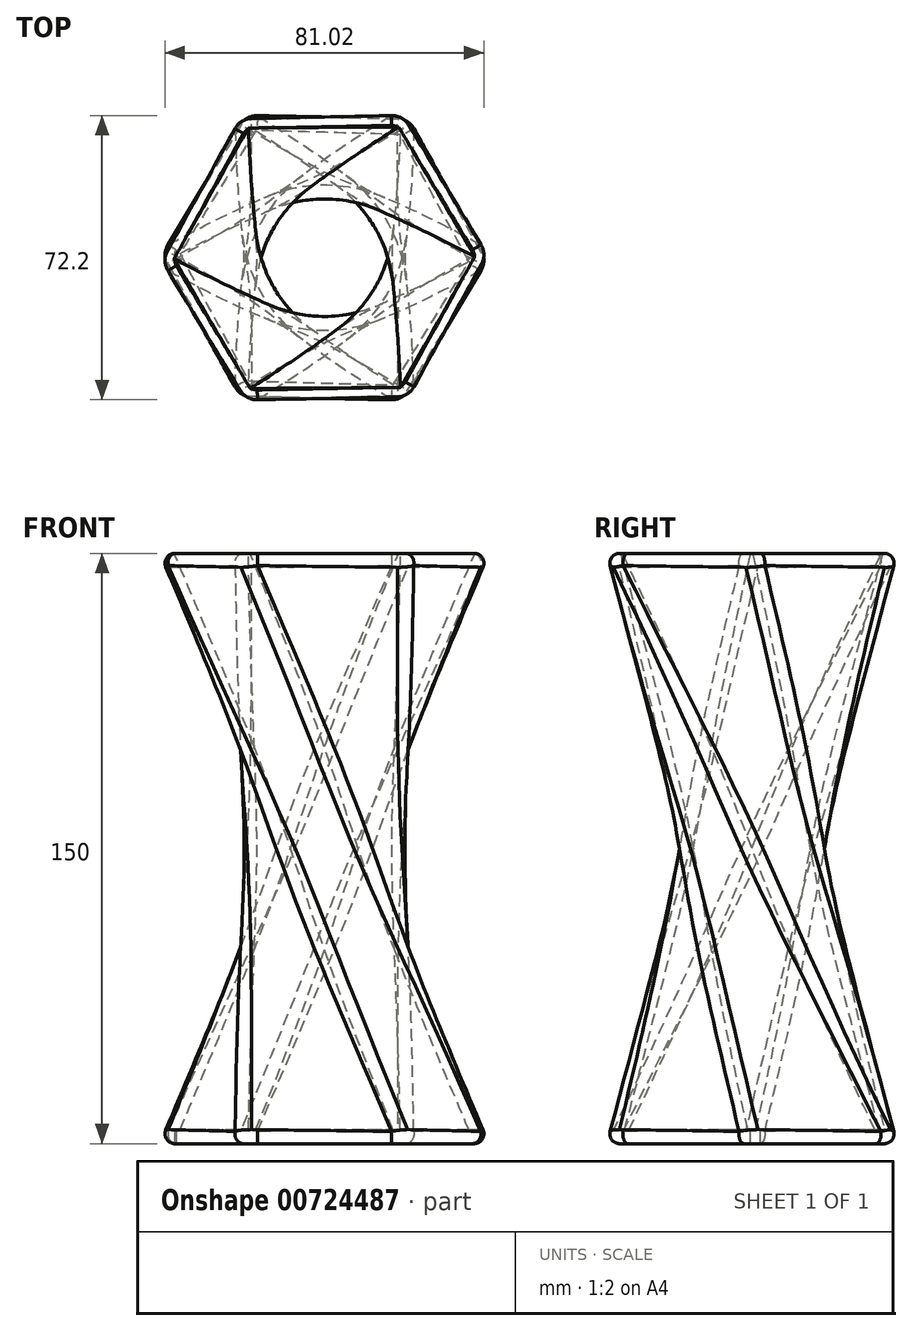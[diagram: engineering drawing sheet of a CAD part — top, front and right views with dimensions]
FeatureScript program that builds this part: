
annotation { "Feature Type Name" : "Feature", "Feature Type Description" : "" }
export const myFeature = defineFeature(function(context is Context, id is Id, definition is map)
    precondition{}
    {
        {
            var Q0;
            Q0=qCreatedBy(makeId("Top.planeOp"),FACE);
            var sketch = newSketch(context, id + "F0", { "sketchPlane" : qUnion([Q0])});
            skLineSegment(sketch, "E0", {"start": v(-43.65, 0) * mm, "end": v(41.43, 0) * mm, "construction": true});
            skLineSegment(sketch, "E1", {"start": v(0, 36.84) * mm, "end": v(0, -39.6) * mm, "construction": true});
            skLineSegment(sketch, "E2", {"start": v(-43.65, 0) * mm, "end": v(-22.38, 36.84) * mm});
            skLineSegment(sketch, "E3", {"start": v(-22.38, 36.84) * mm, "end": v(20.16, 36.84) * mm});
            skLineSegment(sketch, "E4", {"start": v(20.16, 36.84) * mm, "end": v(41.43, 0) * mm});
            skLineSegment(sketch, "E5.MirrorCS", {"start": v(-43.65, 0) * mm, "end": v(-22.38, -36.84) * mm});
            skLineSegment(sketch, "E6.MirrorCS", {"start": v(-22.38, -36.84) * mm, "end": v(20.16, -36.84) * mm});
            skLineSegment(sketch, "E7.MirrorCS", {"start": v(20.16, -36.84) * mm, "end": v(41.43, 0) * mm});
            skSolve(sketch);
        }
        {
            var Q0;
            Q0=qCreatedBy(makeId("Top.planeOp"),FACE);
            cPlane(context, id + "F1", {"entities" : qUnion([Q0]), "cplaneType" : CPlaneType.OFFSET, "offset" : 150 * mm, "width" : 150 * mm, "height" : 150 * mm});
        }
        {
            var Q0;
            Q0=qCreatedBy(id+"F1.planeOp",FACE);
            var sketch = newSketch(context, id + "F2", { "sketchPlane" : qUnion([Q0])});
            skLineSegment(sketch, "E8.0.0", {"start": v(-22.38, -36.84) * mm, "end": v(20.16, -36.84) * mm});
            skLineSegment(sketch, "E8.0.1", {"start": v(20.16, -36.84) * mm, "end": v(41.43, 0) * mm});
            skLineSegment(sketch, "E8.0.2", {"start": v(41.43, 0) * mm, "end": v(20.16, 36.84) * mm});
            skLineSegment(sketch, "E8.0.3", {"start": v(20.16, 36.84) * mm, "end": v(-22.38, 36.84) * mm});
            skLineSegment(sketch, "E8.0.4", {"start": v(-22.38, 36.84) * mm, "end": v(-43.65, 0) * mm});
            skLineSegment(sketch, "E8.0.5", {"start": v(-43.65, 0) * mm, "end": v(-22.38, -36.84) * mm});
            skSolve(sketch);
        }
        {
            var Q0;
            Q0=makeQuery(id+"F0.imprint","IMPRINT",FACE,{"disambiguationData":[TD([[makeQuery(id+"F0.imprint","IMPRINT",EDGE,{"derivedFrom":sQuery(id+"F0.wireOp",EDGE,"E2")}),-1.0]])]});
            var Q1;
            Q1=makeQuery(id+"F2.imprint","IMPRINT",FACE,{"disambiguationData":[TD([[makeQuery(id+"F2.imprint","IMPRINT",EDGE,{"derivedFrom":sQuery(id+"F2.wireOp",EDGE,"E8.0.0")}),1.0]])]});
            var Q2;
            Q2=sQuery(id+"F0.wireOp",VERTEX,"E3.end");
            var Q3;
            Q3=sQuery(id+"F2.wireOp",VERTEX,"E8.0.0.end");
            loft(context, id + "F3", {"sheetProfilesArray" : [{ "sheetProfileEntities" : qUnion([Q0]) }, { "sheetProfileEntities" : qUnion([Q1]) }], "matchConnections" : true, "connections" : [{ "connectionEntities" : qUnion([Q2, Q3]), "connectionEdgeQueries" : qUnion([]), "connectionEdgeParameters" : [] }]});
        }
        {
            var Q0;
            Q0=makeQuery(id+"F3.opLoft","CAP_FACE",FACE,{"disambiguationData":[OSD([makeQuery(id+"F2.imprint","IMPRINT",FACE,{"disambiguationData":[TD([[makeQuery(id+"F2.imprint","IMPRINT",EDGE,{"derivedFrom":sQuery(id+"F2.wireOp",EDGE,"E8.0.0")}),1.0]])]})])],"isStart":true});
            shell(context, id + "F4", {"entities" : qUnion([Q0]), "thickness" : 3.5 * mm});
        }
        {
            var Q0;
            Q0=makeQuery(id+"F3.opLoft","SWEPT_EDGE",EDGE,{"disambiguationData":[OSD([sQuery(id+"F0.wireOp",EDGE,"E4"),sQuery(id+"F0.wireOp",EDGE,"E7.MirrorCS"),sQuery(id+"F2.wireOp",EDGE,"E8.0.0"),sQuery(id+"F2.wireOp",EDGE,"E8.0.5")])]});
            var Q1;
            Q1=makeQuery(id+"F3.opLoft","SWEPT_EDGE",EDGE,{"disambiguationData":[OSD([sQuery(id+"F0.wireOp",EDGE,"E3"),sQuery(id+"F0.wireOp",EDGE,"E4"),sQuery(id+"F2.wireOp",EDGE,"E8.0.0"),sQuery(id+"F2.wireOp",EDGE,"E8.0.1")])]});
            var Q2;
            Q2=makeQuery(id+"F3.opLoft","SWEPT_EDGE",EDGE,{"disambiguationData":[OSD([sQuery(id+"F0.wireOp",EDGE,"E2"),sQuery(id+"F0.wireOp",EDGE,"E3"),sQuery(id+"F2.wireOp",EDGE,"E8.0.1"),sQuery(id+"F2.wireOp",EDGE,"E8.0.2")])]});
            var Q3;
            Q3=makeQuery(id+"F3.opLoft","SWEPT_EDGE",EDGE,{"disambiguationData":[OSD([sQuery(id+"F0.wireOp",EDGE,"E2"),sQuery(id+"F0.wireOp",EDGE,"E5.MirrorCS"),sQuery(id+"F2.wireOp",EDGE,"E8.0.2"),sQuery(id+"F2.wireOp",EDGE,"E8.0.3")])]});
            var Q4;
            Q4=makeQuery(id+"F3.opLoft","SWEPT_EDGE",EDGE,{"disambiguationData":[OSD([sQuery(id+"F0.wireOp",EDGE,"E5.MirrorCS"),sQuery(id+"F0.wireOp",EDGE,"E6.MirrorCS"),sQuery(id+"F2.wireOp",EDGE,"E8.0.3"),sQuery(id+"F2.wireOp",EDGE,"E8.0.4")])]});
            var Q5;
            Q5=makeQuery(id+"F3.opLoft","SWEPT_EDGE",EDGE,{"disambiguationData":[OSD([sQuery(id+"F0.wireOp",EDGE,"E6.MirrorCS"),sQuery(id+"F0.wireOp",EDGE,"E7.MirrorCS"),sQuery(id+"F2.wireOp",EDGE,"E8.0.4"),sQuery(id+"F2.wireOp",EDGE,"E8.0.5")])]});
            fillet(context, id + "F5", {"entities" : qUnion([Q0, Q1, Q2, Q3, Q4, Q5]), "radius" : 5 * mm, "tangentPropagation" : true, "allowEdgeOverflow" : false});
        }
        {
            var Q0;
            Q0=makeQuery(id+"F3.opLoft","MID_CAP_EDGE",EDGE,{"disambiguationData":[OSD([sQuery(id+"F2.wireOp",EDGE,"E8.0.0"),sQuery(id+"F2.wireOp",EDGE,"E8.0.4"),sQuery(id+"F2.wireOp",EDGE,"E8.0.5")])],"capPos":1.0});
            fillet(context, id + "F6", {"entities" : qUnion([Q0]), "radius" : 2.5 * mm, "tangentPropagation" : true, "allowEdgeOverflow" : false});
        }
        {
            var Q0;
            Q0=makeQuery(id+"F3.opLoft","CAP_FACE",FACE,{"disambiguationData":[OSD([makeQuery(id+"F0.imprint","IMPRINT",FACE,{"disambiguationData":[TD([[makeQuery(id+"F0.imprint","IMPRINT",EDGE,{"derivedFrom":sQuery(id+"F0.wireOp",EDGE,"E2")}),-1.0]])]})])],"isStart":true});
            fillet(context, id + "F7", {"entities" : qUnion([Q0]), "radius" : 2.5 * mm, "tangentPropagation" : true, "allowEdgeOverflow" : false});
        }
        {
            var Q0;
            Q0=makeQuery(id+"F3.opLoft","CAP_FACE",FACE,{"disambiguationData":[OSD([makeQuery(id+"F0.imprint","IMPRINT",FACE,{"disambiguationData":[TD([[makeQuery(id+"F0.imprint","IMPRINT",EDGE,{"derivedFrom":sQuery(id+"F0.wireOp",EDGE,"E2")}),-1.0]])]})])],"isStart":true});
            var sketch = newSketch(context, id + "F8", { "sketchPlane" : qUnion([Q0])});
            skFitSpline(sketch, "E9.0.0", {"points": [v(-38.84, 0.42) * mm, v(-38.94, 0.23) * mm, v(-39.05, -0.07) * mm, v(-39.12, -0.5) * mm, v(-39.12, -0.8) * mm, v(-39.09, -1.12) * mm, v(-38.98, -1.54) * mm, v(-38.85, -1.83) * mm, v(-38.74, -2.01) * mm]});
            skFitSpline(sketch, "E9.0.1", {"points": [v(-38.74, -2.01) * mm, v(-32.62, -12.17) * mm, v(-26.49, -22.32) * mm, v(-20.34, -32.46) * mm]});
            skFitSpline(sketch, "E9.0.2", {"points": [v(-20.34, -32.46) * mm, v(-20.23, -32.65) * mm, v(-20.02, -32.9) * mm, v(-19.69, -33.16) * mm, v(-19.42, -33.32) * mm, v(-19.12, -33.45) * mm, v(-18.71, -33.57) * mm, v(-18.4, -33.6) * mm, v(-18.18, -33.6) * mm]});
            skFitSpline(sketch, "E9.0.3", {"points": [v(-18.18, -33.6) * mm, v(-6.32, -33.38) * mm, v(5.53, -33.14) * mm, v(17.4, -32.88) * mm]});
            skFitSpline(sketch, "E9.0.4", {"points": [v(17.4, -32.88) * mm, v(17.6, -32.88) * mm, v(17.92, -32.83) * mm, v(18.32, -32.67) * mm, v(18.6, -32.52) * mm, v(18.85, -32.33) * mm, v(19.16, -32.03) * mm, v(19.35, -31.77) * mm, v(19.45, -31.58) * mm]});
            skFitSpline(sketch, "E9.0.5", {"points": [v(19.45, -31.58) * mm, v(25.19, -21.2) * mm, v(30.9, -10.81) * mm, v(36.62, -0.42) * mm]});
            skFitSpline(sketch, "E9.0.6", {"points": [v(36.62, -0.42) * mm, v(36.72, -0.23) * mm, v(36.83, 0.07) * mm, v(36.9, 0.5) * mm, v(36.9, 0.8) * mm, v(36.87, 1.12) * mm, v(36.76, 1.54) * mm, v(36.63, 1.83) * mm, v(36.52, 2.01) * mm]});
            skFitSpline(sketch, "E9.0.7", {"points": [v(36.52, 2.01) * mm, v(30.4, 12.17) * mm, v(24.27, 22.32) * mm, v(18.12, 32.46) * mm]});
            skFitSpline(sketch, "E9.0.8", {"points": [v(18.12, 32.46) * mm, v(18, 32.65) * mm, v(17.8, 32.9) * mm, v(17.47, 33.16) * mm, v(17.2, 33.32) * mm, v(16.9, 33.45) * mm, v(16.5, 33.57) * mm, v(16.18, 33.6) * mm, v(15.96, 33.6) * mm]});
            skFitSpline(sketch, "E9.0.9", {"points": [v(15.96, 33.6) * mm, v(4.1, 33.38) * mm, v(-7.75, 33.14) * mm, v(-19.61, 32.88) * mm]});
            skFitSpline(sketch, "E9.0.10", {"points": [v(-19.61, 32.88) * mm, v(-19.83, 32.88) * mm, v(-20.14, 32.83) * mm, v(-20.54, 32.67) * mm, v(-20.82, 32.52) * mm, v(-21.07, 32.33) * mm, v(-21.38, 32.03) * mm, v(-21.56, 31.77) * mm, v(-21.67, 31.58) * mm]});
            skFitSpline(sketch, "E9.0.11", {"points": [v(-21.67, 31.58) * mm, v(-27.4, 21.2) * mm, v(-33.13, 10.81) * mm, v(-38.84, 0.42) * mm]});
            skSolve(sketch);
        }
        {
            var Q0;
            Q0=makeQuery(id+"F8.imprint","IMPRINT",FACE,{"disambiguationData":[TD([[makeQuery(id+"F8.imprint","IMPRINT",EDGE,{"derivedFrom":sQuery(id+"F8.wireOp",EDGE,"E9.0.0")}),1.0]])]});
            var Q1;
            Q1=makeQuery(id+"F4.opShell","OFFSET_FACE",FACE,{"disambiguationData":[OSD([makeQuery(id+"F0.imprint","IMPRINT",FACE,{"disambiguationData":[TD([[makeQuery(id+"F0.imprint","IMPRINT",EDGE,{"derivedFrom":sQuery(id+"F0.wireOp",EDGE,"E2")}),-1.0]])]})])]});
            extrude(context, id + "F9", {"entities" : qUnion([Q0]), "operationType" : NewBodyOperationType.REMOVE, "endBound" : BoundingType.UP_TO_SURFACE, "oppositeDirection" : true, "depth" : 1.8 * mm, "endBoundEntityFace" : qUnion([Q1]), "offsetDistance" : 25 * mm});
        }
    });
